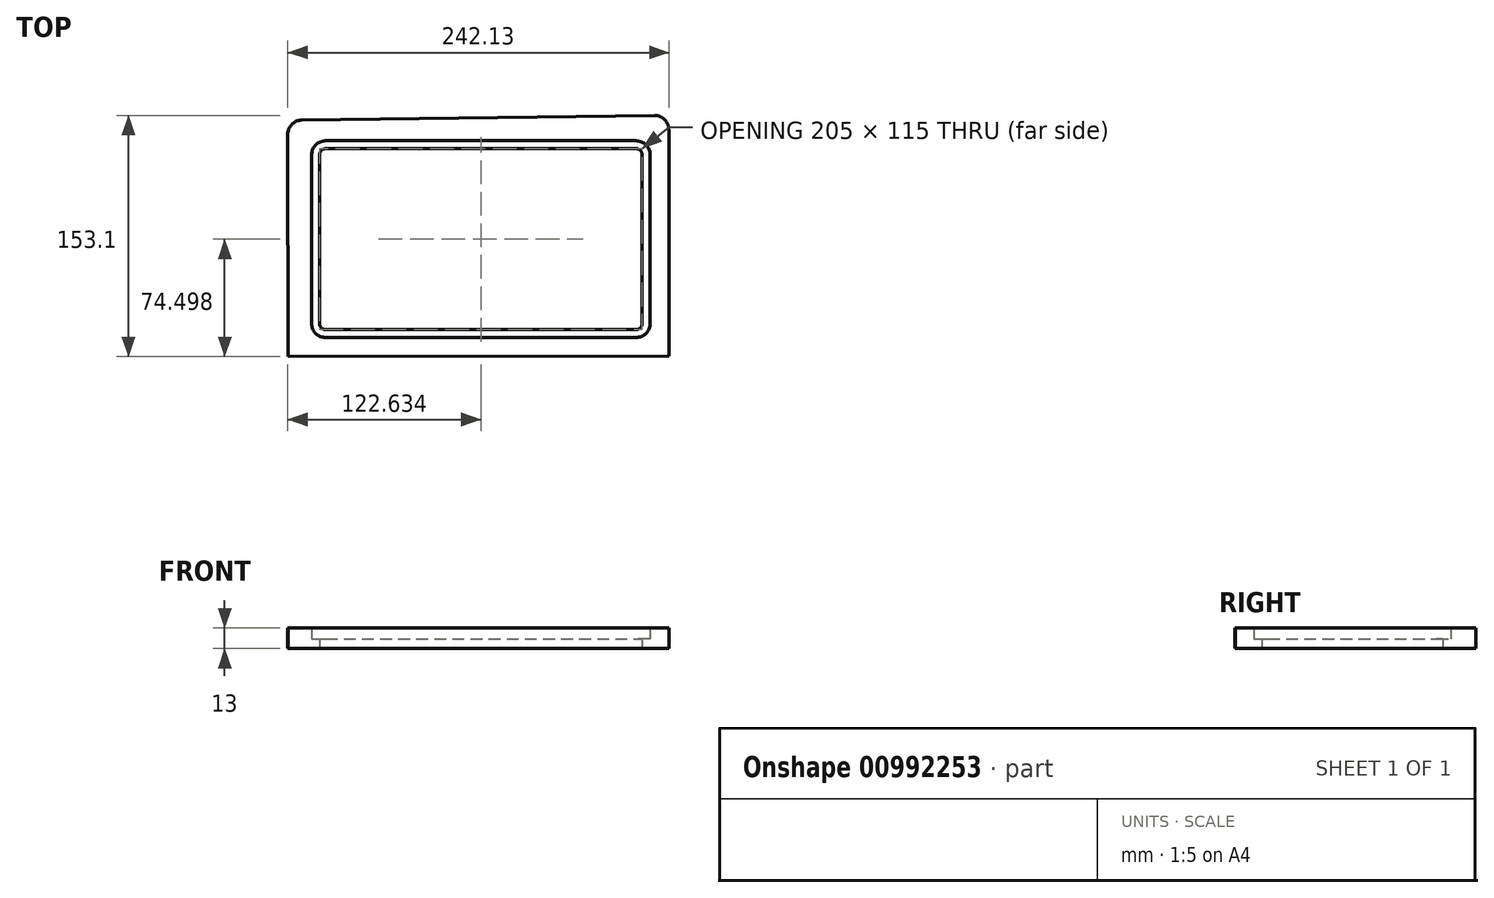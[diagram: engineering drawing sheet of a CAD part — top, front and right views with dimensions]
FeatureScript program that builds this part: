
annotation { "Feature Type Name" : "Feature", "Feature Type Description" : "" }
export const myFeature = defineFeature(function(context is Context, id is Id, definition is map)
    precondition{}
    {
        {
            var Q0;
            Q0=qCreatedBy(makeId("Top.planeOp"),FACE);
            var sketch = newSketch(context, id + "F0", { "sketchPlane" : qUnion([Q0])});
            skLineSegment(sketch, "E0.bottom", {"start": v(-128.1, -75.93) * mm, "end": v(113.9, -75.7) * mm});
            skLineSegment(sketch, "E0.top", {"start": v(-119.35, 74.19) * mm, "end": v(104.65, 77.17) * mm});
            skLineSegment(sketch, "E0.left", {"start": v(-128.1, -75.93) * mm, "end": v(-128.23, 65.18) * mm});
            skLineSegment(sketch, "E0.right", {"start": v(113.9, -75.7) * mm, "end": v(113.77, 68.18) * mm});
            skPoint(sketch, "E1.visualSharp", {"position": v(-128.23, 74.07) * mm});
            skArc(sketch, "E2.filletArc", {"start": v(-119.35, 74.19) * mm, "mid": v(-125.64, 71.5) * mm, "end": v(-128.23, 65.18) * mm});
            skPoint(sketch, "E3.visualSharp", {"position": v(113.76, 77.3) * mm});
            skArc(sketch, "E3.filletArc", {"start": v(113.77, 68.18) * mm, "mid": v(111.09, 74.58) * mm, "end": v(104.65, 77.17) * mm});
            skLineSegment(sketch, "E4.bottom", {"start": v(-104.1, -63.93) * mm, "end": v(92.9, -63.93) * mm});
            skLineSegment(sketch, "E4.top", {"start": v(-104.1, 61.07) * mm, "end": v(92.9, 61.07) * mm});
            skLineSegment(sketch, "E4.left", {"start": v(-113.1, -54.93) * mm, "end": v(-113.1, 52.07) * mm});
            skLineSegment(sketch, "E4.right", {"start": v(101.9, -54.93) * mm, "end": v(101.9, 52.07) * mm});
            skPoint(sketch, "E5.visualSharp", {"position": v(-113.1, 61.07) * mm});
            skArc(sketch, "E5.filletArc", {"start": v(-104.1, 61.07) * mm, "mid": v(-110.46, 58.43) * mm, "end": v(-113.1, 52.07) * mm});
            skPoint(sketch, "E6.visualSharp", {"position": v(101.9, 61.07) * mm});
            skArc(sketch, "E6.filletArc", {"start": v(101.9, 52.07) * mm, "mid": v(99.27, 58.43) * mm, "end": v(92.9, 61.07) * mm});
            skPoint(sketch, "E7.visualSharp", {"position": v(101.9, -63.93) * mm});
            skArc(sketch, "E7.filletArc", {"start": v(92.9, -63.93) * mm, "mid": v(99.27, -61.3) * mm, "end": v(101.9, -54.93) * mm});
            skPoint(sketch, "E8.visualSharp", {"position": v(-113.1, -63.93) * mm});
            skArc(sketch, "E8.filletArc", {"start": v(-113.1, -54.93) * mm, "mid": v(-110.46, -61.3) * mm, "end": v(-104.1, -63.93) * mm});
            skArc(sketch, "E9.0", {"start": v(92.9, -58.93) * mm, "mid": v(95.73, -57.76) * mm, "end": v(96.9, -54.93) * mm});
            skLineSegment(sketch, "E9.1", {"start": v(-104.1, -58.93) * mm, "end": v(92.9, -58.93) * mm});
            skLineSegment(sketch, "E9.2", {"start": v(96.9, -54.93) * mm, "end": v(96.9, 52.07) * mm});
            skArc(sketch, "E9.3", {"start": v(-108.1, -54.93) * mm, "mid": v(-106.92, -57.76) * mm, "end": v(-104.1, -58.93) * mm});
            skArc(sketch, "E9.4", {"start": v(96.9, 52.07) * mm, "mid": v(95.73, 54.9) * mm, "end": v(92.9, 56.07) * mm});
            skLineSegment(sketch, "E9.5", {"start": v(-104.1, 56.07) * mm, "end": v(92.9, 56.07) * mm});
            skArc(sketch, "E9.6", {"start": v(-104.1, 56.07) * mm, "mid": v(-106.92, 54.9) * mm, "end": v(-108.1, 52.07) * mm});
            skLineSegment(sketch, "E9.7", {"start": v(-108.1, -54.93) * mm, "end": v(-108.1, 52.07) * mm});
            skSolve(sketch);
        }
        {
            var Q0;
            Q0=makeQuery(id+"F0.imprint","IMPRINT",FACE,{"disambiguationData":[TD([[makeQuery(id+"F0.imprint","IMPRINT",EDGE,{"derivedFrom":sQuery(id+"F0.wireOp",EDGE,"E0.bottom")}),1.0]])]});
            extrude(context, id + "F1", {"entities" : qUnion([Q0]), "depth" : 13 * mm, "offsetDistance" : 25 * mm});
        }
        {
            var Q0;
            Q0=makeQuery(id+"F0.imprint","IMPRINT",FACE,{"disambiguationData":[TD([[makeQuery(id+"F0.imprint","IMPRINT",EDGE,{"derivedFrom":sQuery(id+"F0.wireOp",EDGE,"E4.bottom")}),1.0]])]});
            extrude(context, id + "F2", {"entities" : qUnion([Q0]), "operationType" : NewBodyOperationType.ADD, "depth" : 6 * mm, "offsetDistance" : 25 * mm});
        }
    });
